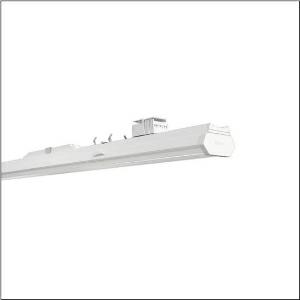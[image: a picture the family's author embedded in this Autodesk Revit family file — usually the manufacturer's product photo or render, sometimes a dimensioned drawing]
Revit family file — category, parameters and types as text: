
# Revit family: licross_r__11_protected_ho_51tp12cn4exm_ba42
name_source: partatom
category: Lighting Fixtures
units: mm (PartAtom-declared; Revit-internal decimal feet)

## family parameters
Cut with Voids When Loaded = No
Host = Face
Light Source = No
Part Type = Normal
Room Calculation Point = No
Round Connector Dimension = Use Diameter
Shared = No

## types (1)
- --- (1 x LED, 14240 lm, 77.6 W, 4000K)
    Apparent Load = 78 VA
    CIE Flux Codes = 70 91 97 98 100
    Color Rendering = 80
    Color Temperature = 4000K
    Default Elevation = 1800 mm
    Description = Licross® 11 Protected HO, luminaire insert, of sheet steel, galvanised, coil coated, white, length: 1.500mm, width: 90mm, height: 101mm, LED rated luminous flux: 14.240lm, light colour: 840, control gear: ON/OFF Multilumen, CLOi, with plug, 3-pole, with phase selection, mains connection: 220..240V, AC, 50/60Hz, start of lifetime: 78W, end of service life: 87W, internal wiring halogen-free, primary light control with lens, of plastic, primary optical cover: cover, of PMMA, light emission: direct distribution, primary light characteristic: symmetric, protection rating (complete): IP64, insulation class (complete): insulation class I (protective earthing), certification: CE, ENEC, VDE, UKCA, protection symbol: D if used in an environment with conductive dust loads with corresponding accessories, impact resistance: IK06, permissible ambient temperature for indoor applications: -35..+35°C, corresponds to IFS (International Featured Standards) requirements for safety and quality in the food industry, reducing of maximum allowable ambient temperature of 5°C with ceiling mounting, LABS conformity tested according to VDMA 24364:2018-05, packaging unit: 1 piece
    Height = 92 mm
    Lamp = 1 x LED
    Lamp Light Flux = 14240 lm
    Lamp Power = 77.6 W
    Lamp count = 1
    Length = 1500 mm
    Luminous efficacy = 184 lm/W
    Manufacturer = Siteco
    ModVariant = No
    Model = 51TP12CN4EXM
    Mounting Place = Ceiling
    Mounting Type = Pendant
    Number of Poles = 1
    OnlyDefault = Yes
    Power Factor = 1
    Product Name = Licross® 11 Protected HO
    Product group = luminaire insert | ceiling pendant
    ProductGroupID = 902
    Protection Class = Protection class I
    Protection Degree = IP 64
    RLX_Detail_Level = 1
    RLX_Emergency_Light_Flux = 0 lm
    RLX_Emergency_Type = 0
    RLX_Emergency_Type_DB = No
    RlxData = <blob elided: 22149 chars, md5=905b769c>
    Socket = socket
    Standby Power = 0 W
    System Light Flux = 14240 lm
    System Power = 78 W
    Type Comments = factory setting: luminous flux: 100 % | (A | C | E) | 181 mA
    Type Image = l_1256148.jpg
    URL = http://relux.com
    VarID = @adj_107457
    Voltage = 0 V
    Weight = 0.00 kg
    Width = 88 mm

## geometry (parser evidence)
native form markers: Blend x4, Sweep x12
no freeform markers — native parametric forms only
